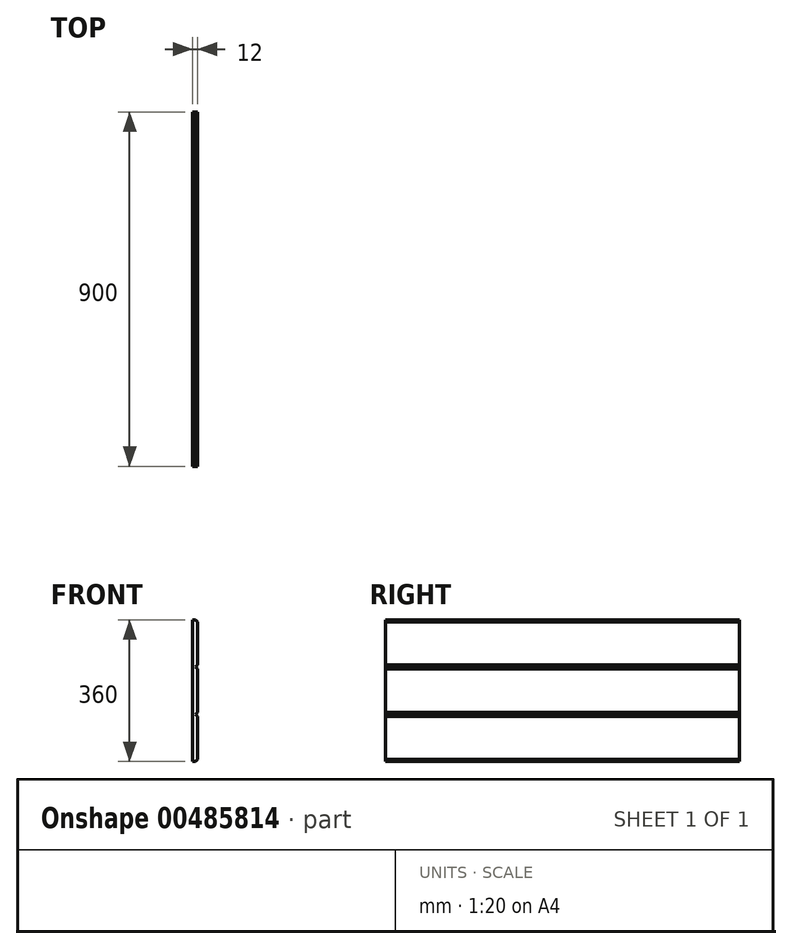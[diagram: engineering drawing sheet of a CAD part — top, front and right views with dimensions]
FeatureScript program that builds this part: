
annotation { "Feature Type Name" : "Feature", "Feature Type Description" : "" }
export const myFeature = defineFeature(function(context is Context, id is Id, definition is map)
    precondition{}
    {
        {
            var Q0;
            Q0=qCreatedBy(makeId("Right.planeOp"),FACE);
            var sketch = newSketch(context, id + "F0", { "sketchPlane" : qUnion([Q0])});
            skLineSegment(sketch, "E0.bottom", {"start": v(-450.7, 187.69) * mm, "end": v(449.3, 187.69) * mm});
            skLineSegment(sketch, "E0.top", {"start": v(-450.7, -172.31) * mm, "end": v(449.3, -172.31) * mm});
            skLineSegment(sketch, "E0.left", {"start": v(-450.7, 187.69) * mm, "end": v(-450.7, -172.31) * mm});
            skLineSegment(sketch, "E0.right", {"start": v(449.3, 187.69) * mm, "end": v(449.3, -172.31) * mm});
            skSolve(sketch);
        }
        {
            var Q0;
            Q0=makeQuery(id+"F0.imprint","IMPRINT",FACE,{"disambiguationData":[TD([[makeQuery(id+"F0.imprint","IMPRINT",EDGE,{"derivedFrom":sQuery(id+"F0.wireOp",EDGE,"E0.bottom")}),-1.0]])]});
            extrude(context, id + "F1", {"entities" : qUnion([Q0]), "depth" : 12 * mm});
        }
        {
            var Q0;
            Q0=makeQuery(id+"F1.opExtrude","SWEPT_FACE",FACE,{"disambiguationData":[OSD([sQuery(id+"F0.wireOp",EDGE,"E0.right")])]});
            var sketch = newSketch(context, id + "F2", { "sketchPlane" : qUnion([Q0])});
            skLineSegment(sketch, "E1", {"start": v(-40.1, -52.31) * mm, "end": v(-40.1, 67.69) * mm, "construction": true});
            skLineSegment(sketch, "E2", {"start": v(-12, -172.31) * mm, "end": v(-7, -172.31) * mm});
            skLineSegment(sketch, "E3", {"start": v(-7, -172.31) * mm, "end": v(-12, -167.31) * mm});
            skLineSegment(sketch, "E4", {"start": v(-12, -167.31) * mm, "end": v(-12, -172.31) * mm});
            skLineSegment(sketch, "E5", {"start": v(-12, -52.31) * mm, "end": v(-12, -57.31) * mm});
            skLineSegment(sketch, "E6", {"start": v(-12, -57.31) * mm, "end": v(-7, -52.31) * mm});
            skLineSegment(sketch, "E7", {"start": v(-7, -52.31) * mm, "end": v(-12, -47.31) * mm});
            skLineSegment(sketch, "E8", {"start": v(-12, -47.31) * mm, "end": v(-12, -52.31) * mm});
            skLineSegment(sketch, "E9", {"start": v(-12, -52.31) * mm, "end": v(-7, -52.31) * mm});
            skLineSegment(sketch, "E10", {"start": v(-12, 67.69) * mm, "end": v(-12, 62.69) * mm});
            skLineSegment(sketch, "E11", {"start": v(-12, 62.69) * mm, "end": v(-7, 67.69) * mm});
            skLineSegment(sketch, "E12", {"start": v(-7, 67.69) * mm, "end": v(-12, 72.69) * mm});
            skLineSegment(sketch, "E13", {"start": v(-12, 72.69) * mm, "end": v(-12, 67.69) * mm});
            skLineSegment(sketch, "E14", {"start": v(-12, 67.69) * mm, "end": v(-7, 67.69) * mm});
            skLineSegment(sketch, "E15", {"start": v(-12, 187.69) * mm, "end": v(-7, 187.69) * mm});
            skLineSegment(sketch, "E16", {"start": v(-7, 187.69) * mm, "end": v(-12, 182.69) * mm});
            skLineSegment(sketch, "E17", {"start": v(-12, 182.69) * mm, "end": v(-12, 187.69) * mm});
            skSolve(sketch);
        }
        {
            var Q0;
            Q0 = qSketchRegion(id + "F2", true);
            extrude(context, id + "F3", {"entities" : qUnion([Q0]), "operationType" : NewBodyOperationType.REMOVE, "endBound" : BoundingType.THROUGH_ALL, "oppositeDirection" : true, "depth" : 25 * mm});
        }
    });
